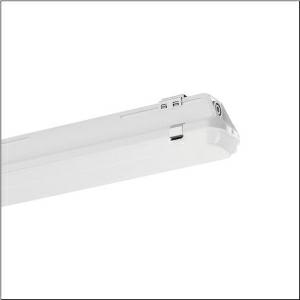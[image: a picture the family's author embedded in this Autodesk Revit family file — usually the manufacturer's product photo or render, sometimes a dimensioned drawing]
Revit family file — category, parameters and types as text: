
# Revit family: monsun_r__21_emergency_51fb107p487c3g_3320
name_source: partatom
category: Lighting Fixtures
units: mm (PartAtom-declared; Revit-internal decimal feet)

## family parameters
Cut with Voids When Loaded = No
Host = Face
Light Source = No
Part Type = Normal
Room Calculation Point = No
Round Connector Dimension = Use Diameter
Shared = No

## types (1)
- --- (1 x LED, 820 lm, 7.1 W, 4000K)
    Apparent Load = 7 VA
    CIE Flux Codes = 47 77 93 94 100
    Color Rendering = 80
    Color Temperature = 4000K
    Default Elevation = 1800 mm
    Description = Monsun® 21 emergency, damp-proof luminaire, chain hanger, primary optical cover: enclosure, of PMMA, light emission: direct distribution, primary light characteristic: symmetric, installation type: suspended mounting, surface-mounted, horizontal mounting, vertical mounting, LED, rated luminous flux: 8.090lm, luminous efficacy: 173lm/W, light colour: 840, colour temperature: 4000K, control gear: ON/OFF, with terminal, 4-pole, max. 2.5mm², mains connection: 220..240V, AC, 50/60Hz, rated input power: 51W, control gear: single battery element, battery: LiFePO4, 9Ah, housing, of glass-fibre reinforced polyester, uncoated, bright grey, incl. chain hanger, length: 1.590mm, width: 90mm, height: 88mm, clip for enclosure, of stainless steel (V2A), ceiling mounting element, of stainless steel (V2A), chain hanger, of stainless steel (V2A), protection rating (complete): IP66, insulation class (complete): insulation class I (protective earthing), certification: CE, UKCA, protection symbol: D, impact resistance: IK04, permissible operating ambient temperature: +5..+25°C, standard: EN 50419, EN 60598-2-1, EN 60598-2-22, corresponds to IFS (International Featured Standards) requirements for safety and quality in the food industry, for indoor or canopied outdoor use, no direct snow, no direct sun, no direct rain, LABS conformity tested according to VDMA 24364:2018-05, contact your sales advisor before using the luminaires in applications with unclear chemical exposure, large temperature fluctuations or condensation-forming humidity, packaging unit: 1 piece
    Height = 89 mm
    Lamp = 1 x LED
    Lamp Light Flux = 820 lm
    Lamp Power = 7.1 W
    Lamp count = 1
    Length = 1590 mm
    Luminous efficacy = 115 lm/W
    Manufacturer = Siteco
    ModVariant = No
    Model = 51FB107P487C3G
    Mounting Place = Ceiling
    Mounting Type = Surface mounted
    Number of Poles = 1
    OnlyDefault = Yes
    Power Factor = 1
    Product Name = Monsun® 21 emergency
    Product group = damp-proof luminaire
    ProductGroupID = 301
    Protection Class = Protection class I
    Protection Degree = IP 66
    RLX_Detail_Level = 1
    RLX_Emergency_Light_Flux = 0 lm
    RLX_Emergency_Type = 0
    RLX_Emergency_Type_DB = No
    RlxData = <blob elided: 88989 chars, md5=9c465927>
    Socket = socket
    Standby Power = 0 W
    System Light Flux = 820 lm
    System Power = 7 W
    Type Comments = : emergency light operation: 3 h
    Type Image = l_1319656.jpg
    URL = http://relux.com
    VarID = @adj_051767
    Voltage = 0 V
    Weight = 0.00 kg
    Width = 90 mm

## geometry (parser evidence)
native form markers: Blend x4, Sweep x13
no freeform markers — native parametric forms only
